# Revit family: TD92_CON720_MAR050_RVT20_R00
name_source: partatom
category: Mobiliário
units: mm (PartAtom-declared; Revit-internal decimal feet)

## family parameters
Com base no plano de trabalho = Não
Compartilhado = Não
Corte com vazios quando carregada = Não
Número OmniClass = 23.40.20.00
Ponto de cálculo do ambiente = Não
Sempre na vertical = Sim
Título OmniClass = General Furniture and Specialties

## types (1)
- TD92_CON720_MAR050_RVT20_R00
    Descrição = Uma bela e elegante mesa de centro entrega elegância a qualquer decoração, dando muito mais beleza aos ambientes. Aproveite agora mesmo para ter uma Mesa de Centro Tramontina Cona em Polietileno. Perfeita para qualquer espaço, ela tem design diferenciado, é sofisticada, além de ser fabricada em polietileno rotomoldado. Você não pode ficar sem todos esses atributos que vão deixar seu ambiente muito mais especial.
    Elevação padrão = 0  [stored 0 ft]
    Fabricante = Tramontina Delta S/A
    Modelo = Mesa de Centro Tramontina Cona em Polietileno Marsala
    Nota-chave = 92720050
    URL = https://www.tramontinastore.com

note: [stored X ft] marks values corroborated as IEEE doubles in the binary element streams (Revit-internal decimal feet)
